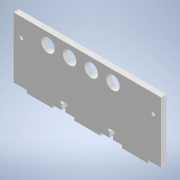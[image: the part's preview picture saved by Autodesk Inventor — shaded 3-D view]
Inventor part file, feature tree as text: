
AUTODESK INVENTOR PART (.ipt)
format: ipt  version: 2022 (Build 260153000, 153)  size: 158,208 bytes
history: native  units: mm
features: other x2, extrude x1, sketch x1, reference x1
ambient origin geometry x8: Origin, YZ Plane, XZ Plane, XY Plane, X Axis, Y Axis, Z Axis, Center Point
bodies: Solid1 (feature_tree)
feature tree (5):
  extrude  "Extrusion1"  Depth=6.2mm
  sketch  "Sketch1"  dims[d0=25.0mm d1=25.0mm d2=25.0mm d3=70.0mm d4=6.2mm d5=0.0mm]
  reference  "Reference1"
  other  "Caja_Reductora_.iam"
  other  "Carcasa_CajaR_Lateral1:1"
